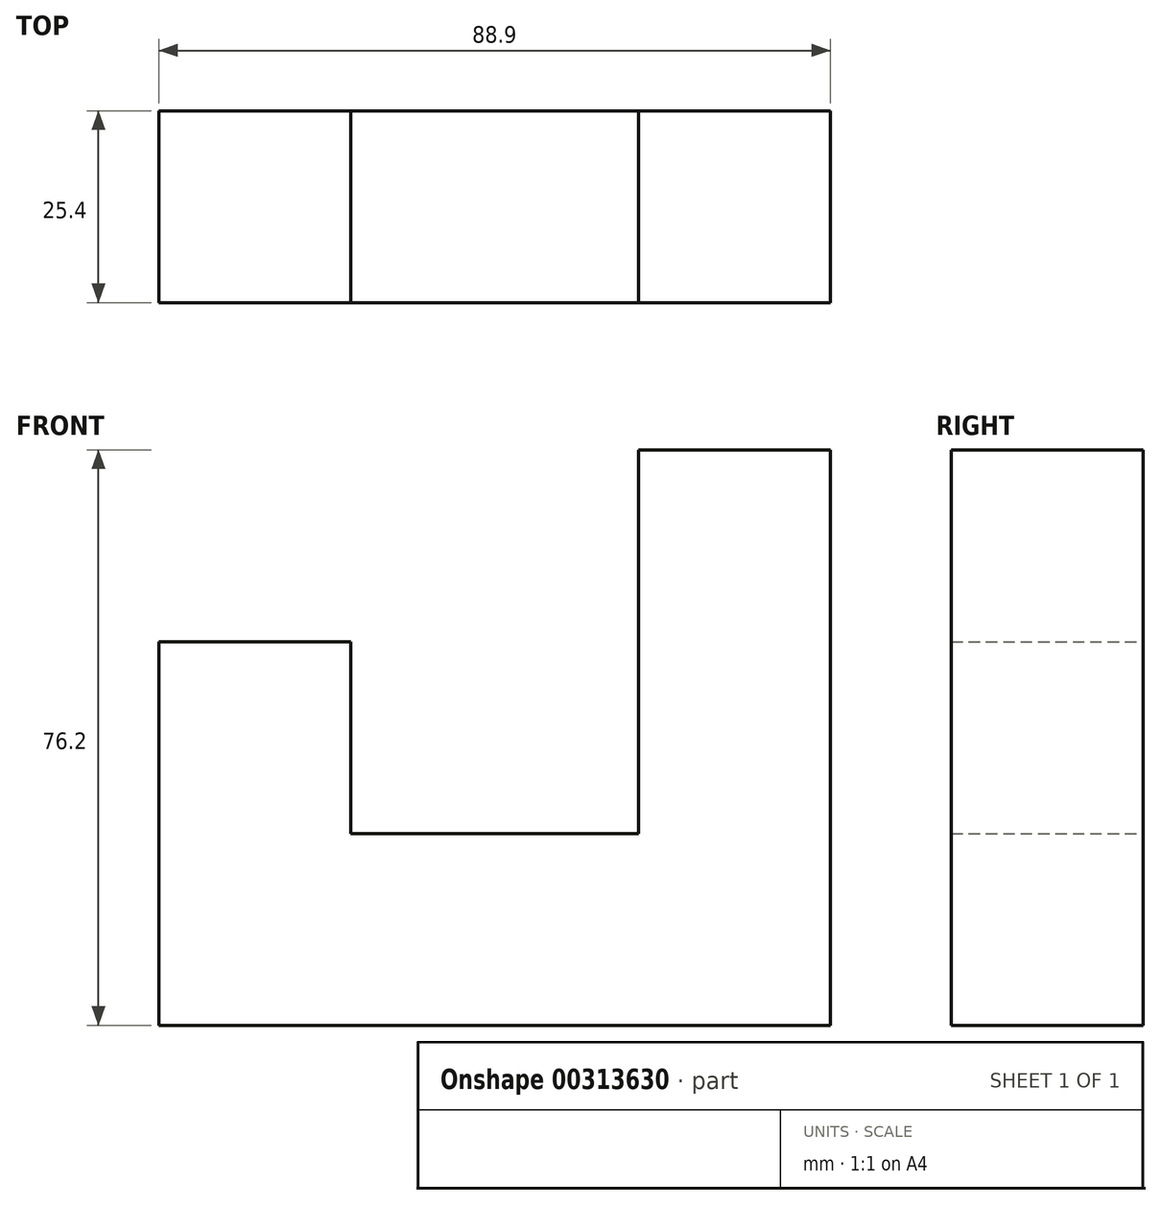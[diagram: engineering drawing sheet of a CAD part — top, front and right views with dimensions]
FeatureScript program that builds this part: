
annotation { "Feature Type Name" : "Feature", "Feature Type Description" : "" }
export const myFeature = defineFeature(function(context is Context, id is Id, definition is map)
    precondition{}
    {
        {
            var Q0;
            Q0=qCreatedBy(makeId("Front.planeOp"),FACE);
            var sketch = newSketch(context, id + "F0", { "sketchPlane" : qUnion([Q0])});
            skLineSegment(sketch, "E0", {"start": v(-38.68, -49.84) * mm, "end": v(50.22, -49.84) * mm});
            skLineSegment(sketch, "E1", {"start": v(50.22, -49.84) * mm, "end": v(50.22, 26.36) * mm});
            skLineSegment(sketch, "E2", {"start": v(50.22, 26.36) * mm, "end": v(24.82, 26.36) * mm});
            skLineSegment(sketch, "E3", {"start": v(24.82, 26.36) * mm, "end": v(24.82, -24.44) * mm});
            skLineSegment(sketch, "E4", {"start": v(24.82, -24.44) * mm, "end": v(-13.28, -24.44) * mm});
            skLineSegment(sketch, "E5", {"start": v(-13.28, -24.44) * mm, "end": v(-13.28, 0.96) * mm});
            skLineSegment(sketch, "E6", {"start": v(-13.28, 0.96) * mm, "end": v(-38.68, 0.96) * mm});
            skLineSegment(sketch, "E7", {"start": v(-38.68, 0.96) * mm, "end": v(-38.68, -49.84) * mm});
            skSolve(sketch);
        }
        {
            var Q0;
            Q0=makeQuery(id+"F0.imprint","IMPRINT",FACE,{"disambiguationData":[TD([[makeQuery(id+"F0.imprint","IMPRINT",EDGE,{"derivedFrom":sQuery(id+"F0.wireOp",EDGE,"E0")}),1.0]])]});
            extrude(context, id + "F1", {"entities" : qUnion([Q0]), "depth" : 25.4 * mm});
        }
    });
